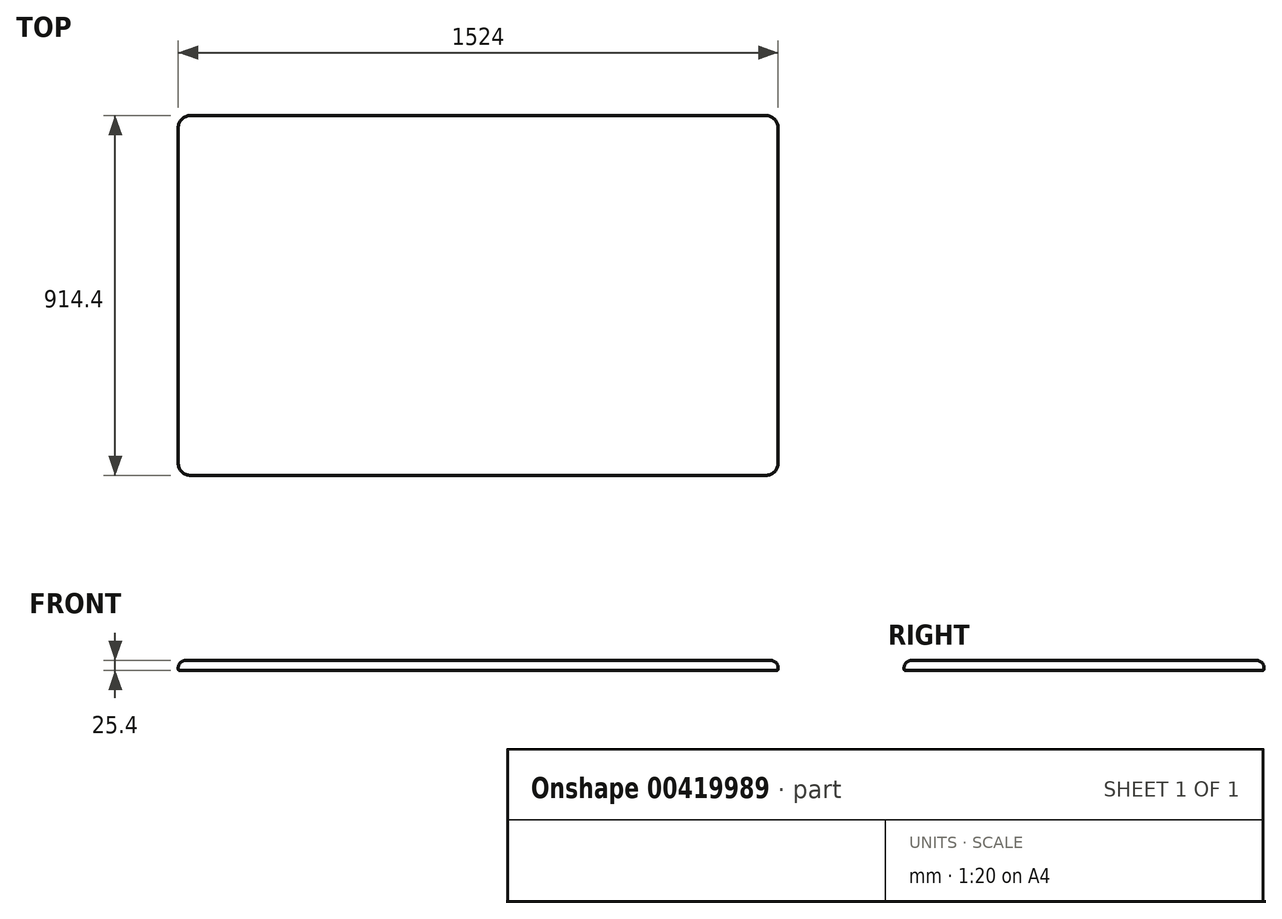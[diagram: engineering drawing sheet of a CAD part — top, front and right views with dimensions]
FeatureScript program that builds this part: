
annotation { "Feature Type Name" : "Feature", "Feature Type Description" : "" }
export const myFeature = defineFeature(function(context is Context, id is Id, definition is map)
    precondition{}
    {
        {
            var Q0;
            Q0=qCreatedBy(makeId("Top.planeOp"),FACE);
            var sketch = newSketch(context, id + "F0", { "sketchPlane" : qUnion([Q0])});
            skLineSegment(sketch, "E0.bottom", {"start": v(31.75, 0) * mm, "end": v(1492.25, 0) * mm});
            skLineSegment(sketch, "E0.top", {"start": v(31.75, 914.4) * mm, "end": v(1492.25, 914.4) * mm});
            skLineSegment(sketch, "E0.left", {"start": v(0, 31.75) * mm, "end": v(0, 882.65) * mm});
            skLineSegment(sketch, "E0.right", {"start": v(1524, 31.75) * mm, "end": v(1524, 882.65) * mm});
            skPoint(sketch, "E1.visualSharp", {"position": v(0, 914.4) * mm});
            skArc(sketch, "E1.filletArc", {"start": v(31.75, 914.4) * mm, "mid": v(9.3, 905.1) * mm, "end": v(0, 882.65) * mm});
            skPoint(sketch, "E2.visualSharp", {"position": v(1524, 914.4) * mm});
            skArc(sketch, "E2.filletArc", {"start": v(1524, 882.65) * mm, "mid": v(1514.7, 905.1) * mm, "end": v(1492.25, 914.4) * mm});
            skPoint(sketch, "E3.visualSharp", {"position": v(1524, 0) * mm});
            skArc(sketch, "E3.filletArc", {"start": v(1492.25, 0) * mm, "mid": v(1514.7, 9.3) * mm, "end": v(1524, 31.75) * mm});
            skPoint(sketch, "E4.visualSharp", {"position": v(0, 0) * mm});
            skArc(sketch, "E4.filletArc", {"start": v(0, 31.75) * mm, "mid": v(9.3, 9.3) * mm, "end": v(31.75, 0) * mm});
            skSolve(sketch);
        }
        {
            var Q0;
            Q0=makeQuery(id+"F0.imprint","IMPRINT",FACE,{"disambiguationData":[TD([[makeQuery(id+"F0.imprint","IMPRINT",EDGE,{"derivedFrom":sQuery(id+"F0.wireOp",EDGE,"E0.bottom")}),1.0]])]});
            extrude(context, id + "F1", {"entities" : qUnion([Q0]), "depth" : 25.4 * mm});
        }
        {
            var Q0;
            Q0=makeQuery(id+"F1.opExtrude","CAP_EDGE",EDGE,{"disambiguationData":[OSD([sQuery(id+"F0.wireOp",EDGE,"E0.bottom")])],"isStart":true});
            fillet(context, id + "F2", {"entities" : qUnion([Q0]), "radius" : 3.17 * mm, "tangentPropagation" : true, "allowEdgeOverflow" : false});
        }
        {
            var Q0;
            Q0=makeQuery(id+"F1.opExtrude","CAP_EDGE",EDGE,{"disambiguationData":[OSD([sQuery(id+"F0.wireOp",EDGE,"E0.bottom")])],"isStart":false});
            fillet(context, id + "F3", {"entities" : qUnion([Q0]), "radius" : 19.05 * mm, "tangentPropagation" : true, "allowEdgeOverflow" : false});
        }
    });
